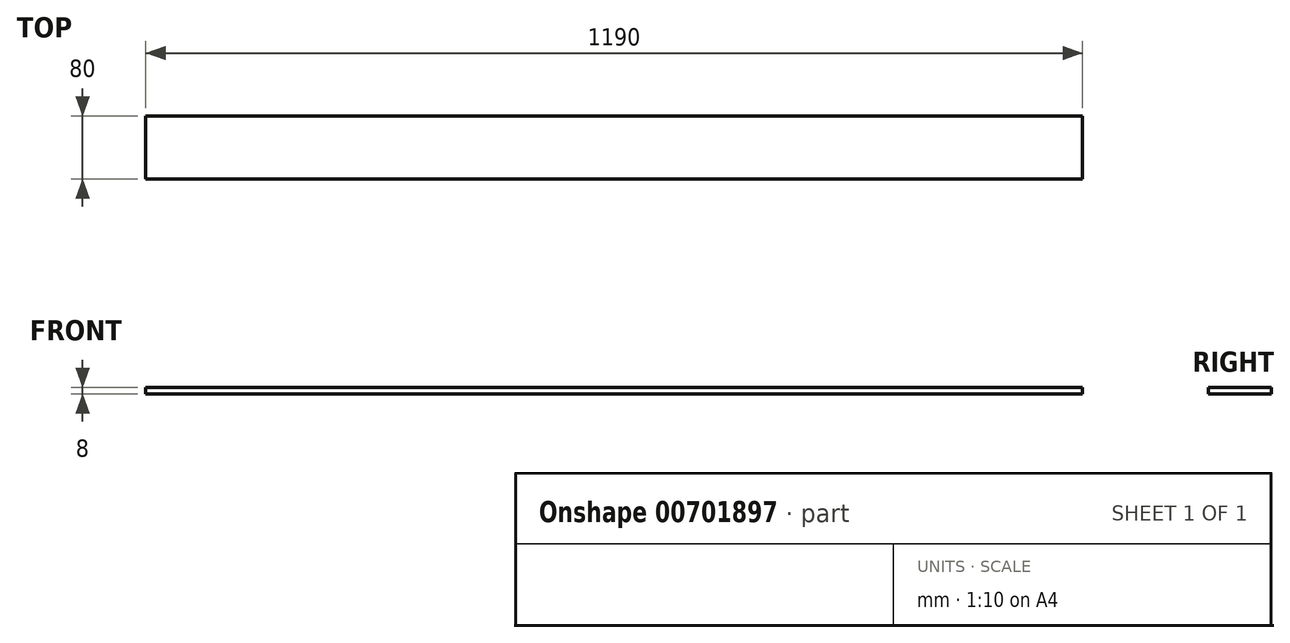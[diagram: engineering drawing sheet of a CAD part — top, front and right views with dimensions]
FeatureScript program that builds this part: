
annotation { "Feature Type Name" : "Feature", "Feature Type Description" : "" }
export const myFeature = defineFeature(function(context is Context, id is Id, definition is map)
    precondition{}
    {
        {
            var Q0;
            Q0=qCreatedBy(makeId("Top.planeOp"),FACE);
            var sketch = newSketch(context, id + "F0", { "sketchPlane" : qUnion([Q0])});
            skLineSegment(sketch, "E0.bottom", {"start": v(0, 0) * mm, "end": v(1190, 0) * mm});
            skLineSegment(sketch, "E0.top", {"start": v(0, 80) * mm, "end": v(1190, 80) * mm});
            skLineSegment(sketch, "E0.left", {"start": v(0, 0) * mm, "end": v(0, 80) * mm});
            skLineSegment(sketch, "E0.right", {"start": v(1190, 0) * mm, "end": v(1190, 80) * mm});
            skSolve(sketch);
        }
        {
            var Q0;
            Q0=makeQuery(id+"F0.imprint","IMPRINT",FACE,{"disambiguationData":[TD([[makeQuery(id+"F0.imprint","IMPRINT",EDGE,{"derivedFrom":sQuery(id+"F0.wireOp",EDGE,"E0.bottom")}),1.0]])]});
            extrude(context, id + "F1", {"entities" : qUnion([Q0]), "depth" : 8 * mm, "offsetDistance" : 25 * mm});
        }
    });
